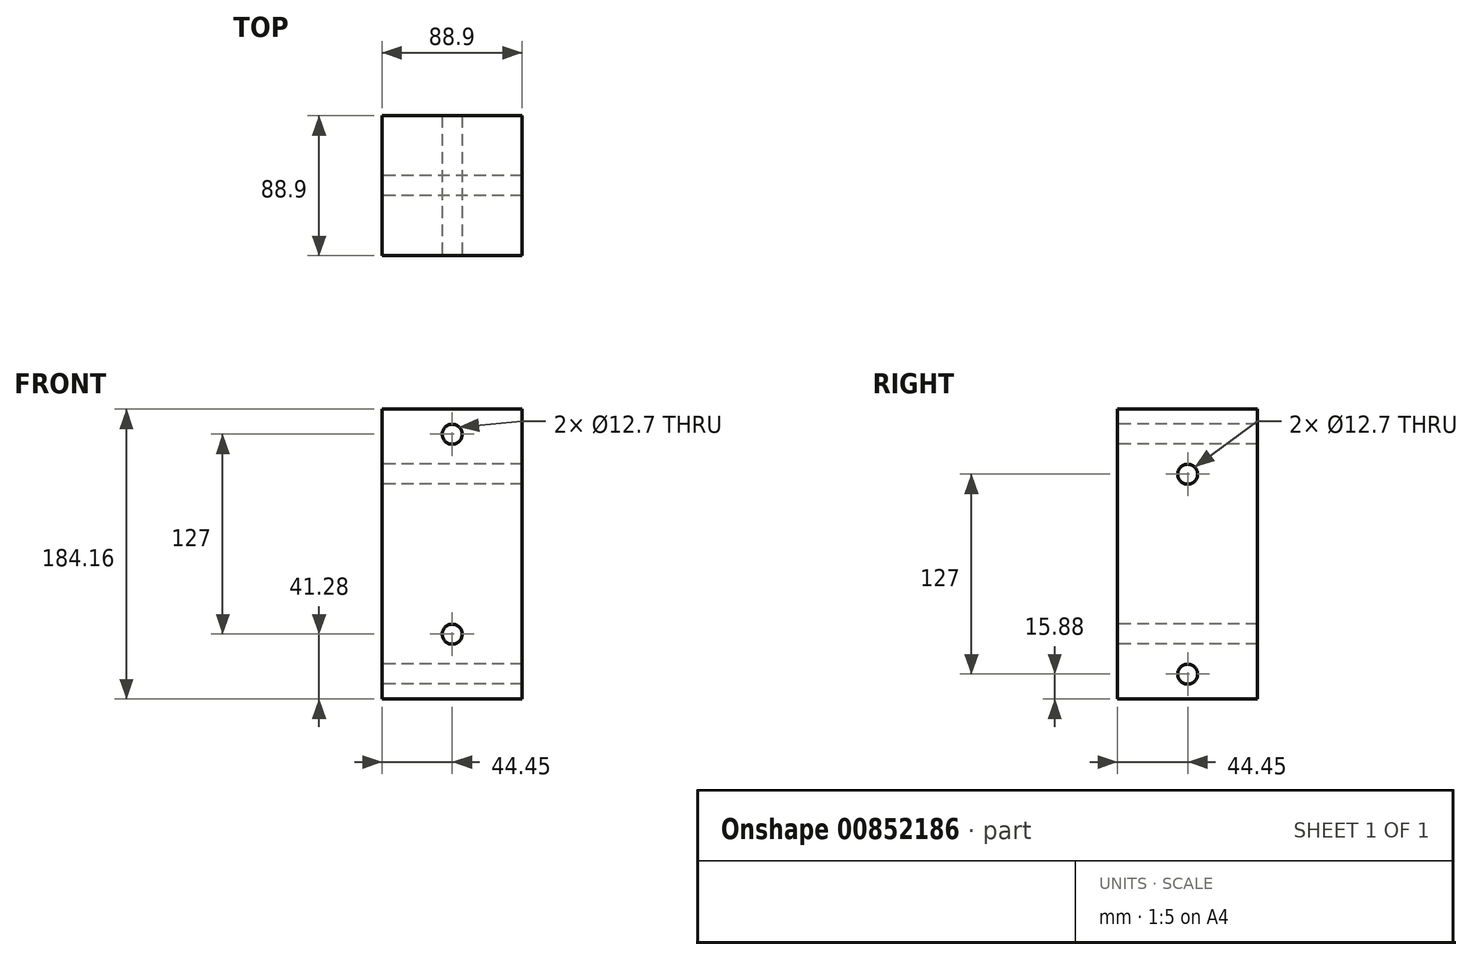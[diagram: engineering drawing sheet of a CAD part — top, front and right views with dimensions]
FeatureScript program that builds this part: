
annotation { "Feature Type Name" : "Feature", "Feature Type Description" : "" }
export const myFeature = defineFeature(function(context is Context, id is Id, definition is map)
    precondition{}
    {
        {
            var Q0;
            Q0=qCreatedBy(makeId("Top.planeOp"),FACE);
            var sketch = newSketch(context, id + "F0", { "sketchPlane" : qUnion([Q0])});
            skLineSegment(sketch, "E0.bottom", {"start": v(44.45, -44.45) * mm, "end": v(-44.45, -44.45) * mm});
            skLineSegment(sketch, "E0.top", {"start": v(44.45, 44.45) * mm, "end": v(-44.45, 44.45) * mm});
            skLineSegment(sketch, "E0.left", {"start": v(44.45, -44.45) * mm, "end": v(44.45, 44.45) * mm});
            skLineSegment(sketch, "E0.right", {"start": v(-44.45, -44.45) * mm, "end": v(-44.45, 44.45) * mm});
            skPoint(sketch, "E0.middle", {"position": v(0, 0) * mm});
            skSolve(sketch);
        }
        {
            var Q0;
            Q0 = qSketchRegion(id + "F0", true);
            extrude(context, id + "F1", {"entities" : qUnion([Q0]), "endBound" : BoundingType.SYMMETRIC, "depth" : 184.15 * mm, "offsetDistance" : 25.4 * mm});
        }
        {
            var Q0;
            Q0=qCreatedBy(makeId("Front.planeOp"),FACE);
            var sketch = newSketch(context, id + "F2", { "sketchPlane" : qUnion([Q0])});
            skLineSegment(sketch, "E1", {"start": v(0, 0) * mm, "end": v(0, 12.7) * mm, "construction": true});
            skLineSegment(sketch, "E2", {"start": v(0, -50.8) * mm, "end": v(0, 76.2) * mm, "construction": true});
            skCircle(sketch, "E3", {"center": v(0, 76.2) * mm, "radius": 6.35 * mm});
            skCircle(sketch, "E4", {"center": v(0, -50.8) * mm, "radius": 6.35 * mm});
            skSolve(sketch);
        }
        {
            var Q0;
            Q0 = qSketchRegion(id + "F2", true);
            extrude(context, id + "F3", {"entities" : qUnion([Q0]), "operationType" : NewBodyOperationType.REMOVE, "endBound" : BoundingType.SYMMETRIC, "oppositeDirection" : true, "depth" : 101.6 * mm, "offsetDistance" : 25.4 * mm});
        }
        {
            var Q0;
            Q0=qCreatedBy(makeId("Right.planeOp"),FACE);
            var sketch = newSketch(context, id + "F4", { "sketchPlane" : qUnion([Q0])});
            skLineSegment(sketch, "E5", {"start": v(0, 0) * mm, "end": v(0, -12.7) * mm, "construction": true});
            skLineSegment(sketch, "E6", {"start": v(0, 50.8) * mm, "end": v(0, -76.2) * mm, "construction": true});
            skCircle(sketch, "E7", {"center": v(0, 50.8) * mm, "radius": 6.35 * mm});
            skCircle(sketch, "E8", {"center": v(0, -76.2) * mm, "radius": 6.35 * mm});
            skSolve(sketch);
        }
        {
            var Q0;
            Q0 = qSketchRegion(id + "F4", true);
            extrude(context, id + "F5", {"entities" : qUnion([Q0]), "operationType" : NewBodyOperationType.REMOVE, "endBound" : BoundingType.SYMMETRIC, "depth" : 101.6 * mm, "offsetDistance" : 25.4 * mm});
        }
    });
